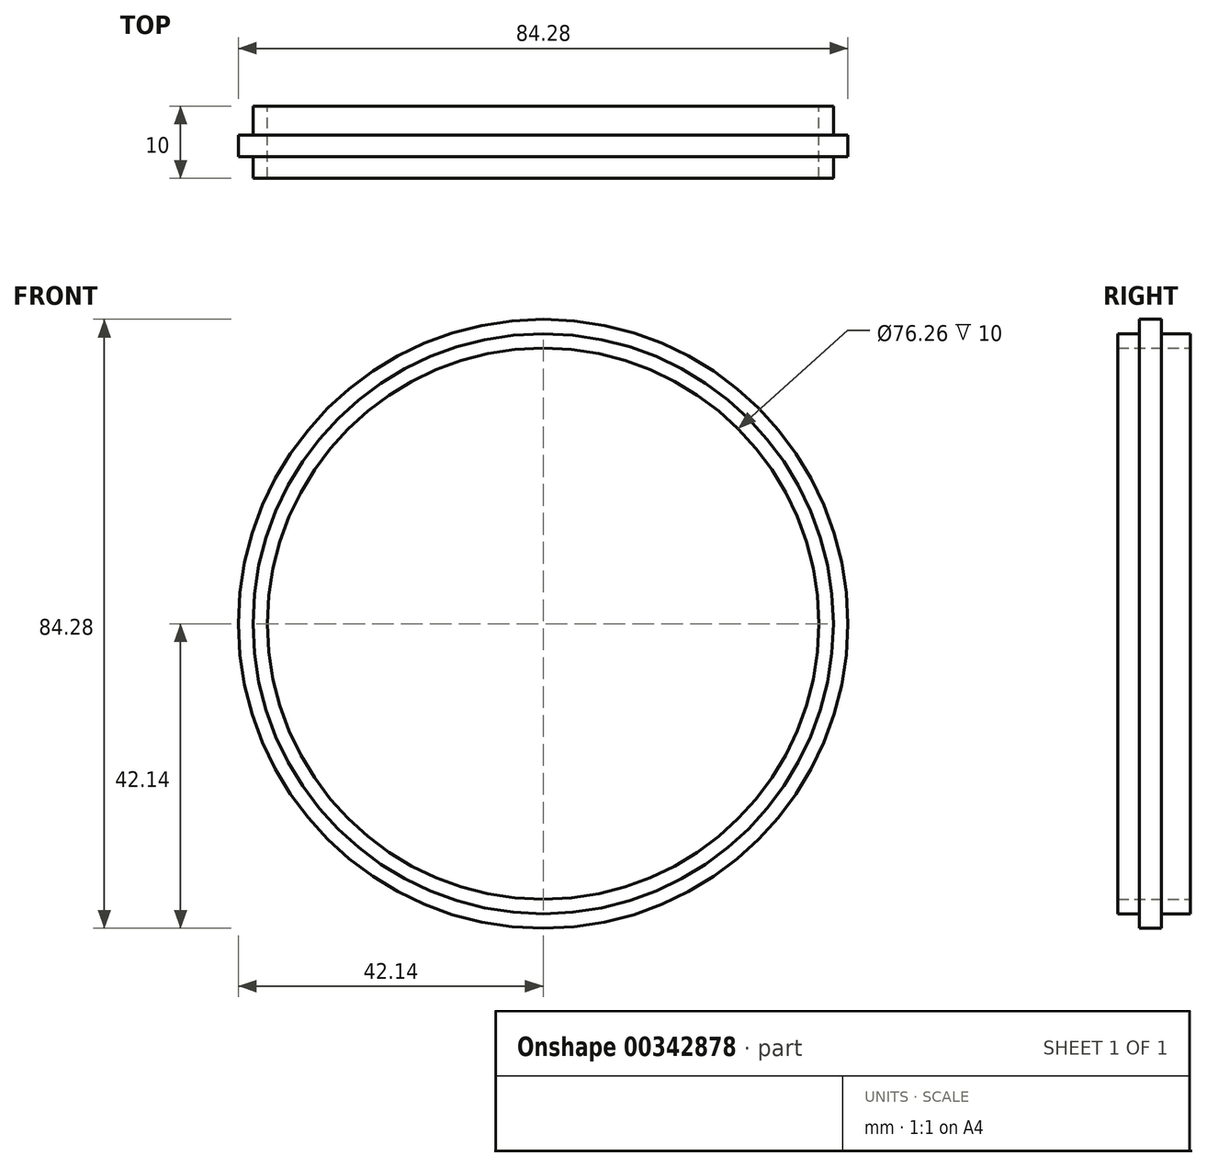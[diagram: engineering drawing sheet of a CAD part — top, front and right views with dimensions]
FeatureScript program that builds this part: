
annotation { "Feature Type Name" : "Feature", "Feature Type Description" : "" }
export const myFeature = defineFeature(function(context is Context, id is Id, definition is map)
    precondition{}
    {
        {
            var Q0;
            Q0=qCreatedBy(makeId("Front.planeOp"),FACE);
            var sketch = newSketch(context, id + "F0", { "sketchPlane" : qUnion([Q0])});
            skCircle(sketch, "E0", {"center": v(0, 0) * mm, "radius": 44.45 * mm, "construction": true});
            skLineSegment(sketch, "E1", {"start": v(0, 0) * mm, "end": v(-31.43, 31.43) * mm, "construction": true});
            skCircle(sketch, "E2", {"center": v(-31.43, 31.43) * mm, "radius": 2.15 * mm});
            skCircle(sketch, "E3.1.0", {"center": v(-31.43, -31.43) * mm, "radius": 2.15 * mm});
            skCircle(sketch, "E3.2.0", {"center": v(31.43, -31.43) * mm, "radius": 2.15 * mm});
            skCircle(sketch, "E3.3.0", {"center": v(31.43, 31.43) * mm, "radius": 2.15 * mm});
            skLineSegment(sketch, "E4.bottom", {"start": v(45.09, 45.09) * mm, "end": v(-45.08, 45.09) * mm, "construction": true});
            skLineSegment(sketch, "E4.top", {"start": v(45.09, -45.09) * mm, "end": v(-45.09, -45.09) * mm, "construction": true});
            skLineSegment(sketch, "E4.left", {"start": v(45.09, 45.09) * mm, "end": v(45.09, -45.09) * mm, "construction": true});
            skLineSegment(sketch, "E4.right", {"start": v(-45.09, 45.09) * mm, "end": v(-45.09, -45.09) * mm, "construction": true});
            skLineSegment(sketch, "E5", {"start": v(0, 0) * mm, "end": v(-37.48, -37.48) * mm, "construction": true});
            skCircle(sketch, "E6.converted", {"center": v(0, 0) * mm, "radius": 38.13 * mm});
            skCircle(sketch, "E7.converted", {"center": v(0, 0) * mm, "radius": 40.13 * mm});
            skSolve(sketch);
        }
        {
            var Q0;
            Q0=makeQuery(id+"F0.imprint","IMPRINT",FACE,{"disambiguationData":[TD([[makeQuery(id+"F0.imprint","IMPRINT",EDGE,{"derivedFrom":sQuery(id+"F0.wireOp",EDGE,"E6.converted")}),-1.0]])]});
            extrude(context, id + "F1", {"entities" : qUnion([Q0]), "depth" : 10 * mm});
        }
        {
            var Q0;
            Q0=makeQuery(id+"F1.opExtrude","CAP_FACE",FACE,{"disambiguationData":[OSD([sQuery(id+"F0.wireOp",EDGE,"E6.converted"),sQuery(id+"F0.wireOp",EDGE,"E7.converted")])],"isStart":false});
            cPlane(context, id + "F2", {"entities" : qUnion([Q0]), "cplaneType" : CPlaneType.OFFSET, "offset" : 3 * mm, "oppositeDirection" : true, "width" : 150 * mm, "height" : 150 * mm});
        }
        {
            var Q0;
            Q0=qCreatedBy(id+"F2.planeOp",FACE);
            var sketch = newSketch(context, id + "F3", { "sketchPlane" : qUnion([Q0])});
            skCircle(sketch, "E8", {"center": v(0, 0) * mm, "radius": 42.14 * mm});
            skCircle(sketch, "E9", {"center": v(0, 0) * mm, "radius": 40.13 * mm});
            skSolve(sketch);
        }
        {
            var Q0;
            Q0=makeQuery(id+"F3.imprint","IMPRINT",FACE,{"disambiguationData":[TD([[makeQuery(id+"F3.imprint","IMPRINT",EDGE,{"derivedFrom":sQuery(id+"F3.wireOp",EDGE,"E8")}),1.0]])]});
            extrude(context, id + "F4", {"entities" : qUnion([Q0]), "operationType" : NewBodyOperationType.ADD, "flatOperationType" : FlatOperationType.REMOVE, "oppositeDirection" : true, "offsetDistance" : 25 * mm, "depth" : 3 * mm, "domain" : OperationDomain.MODEL});
        }
    });
